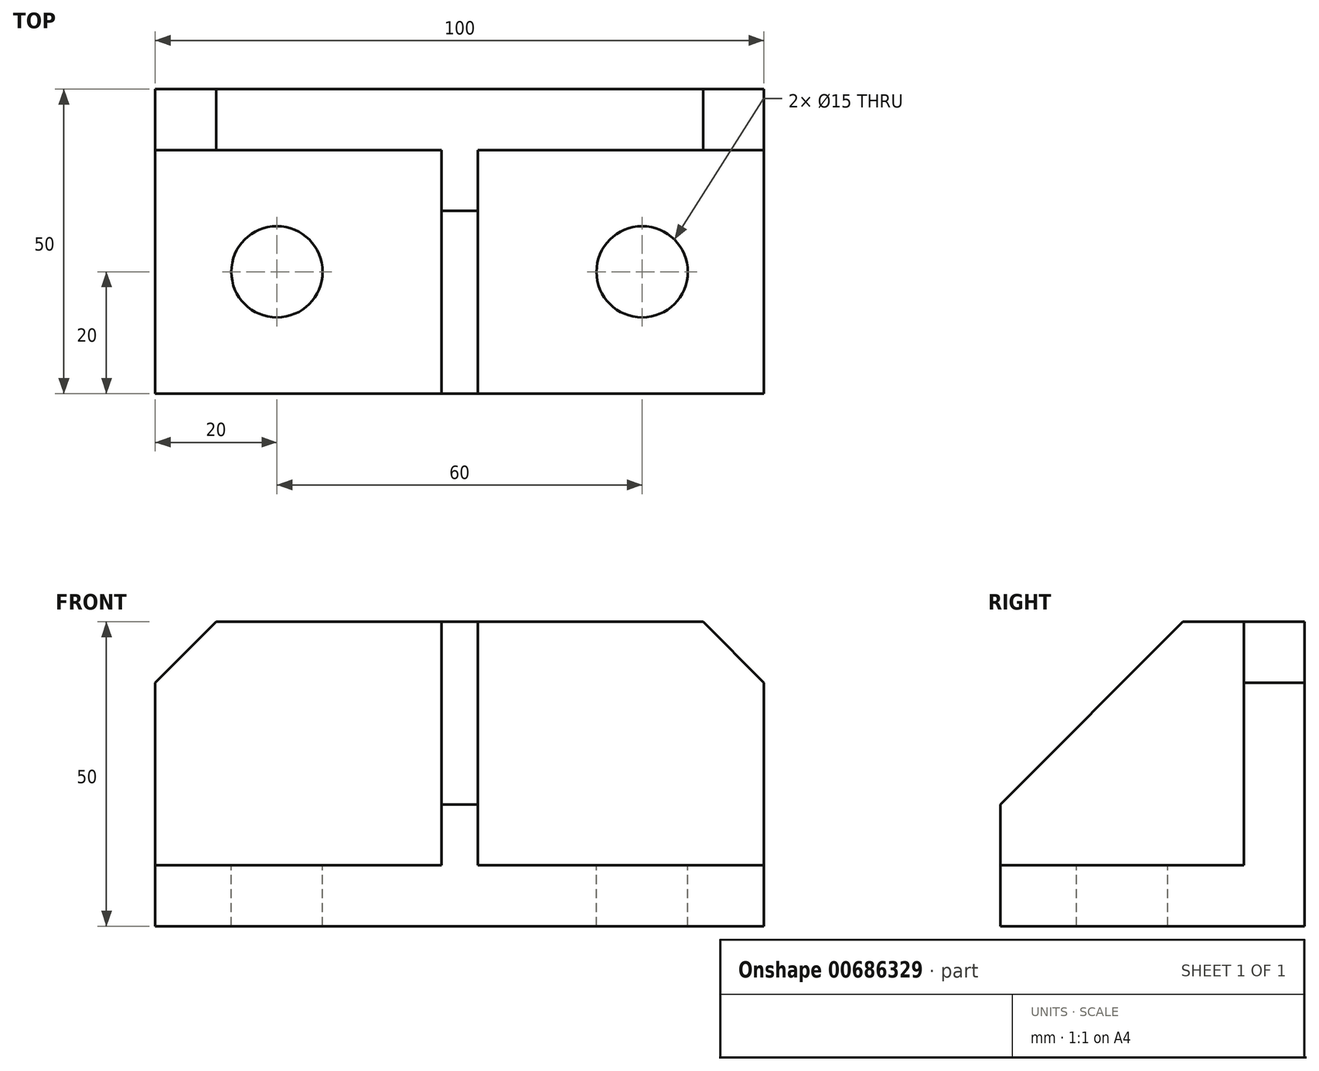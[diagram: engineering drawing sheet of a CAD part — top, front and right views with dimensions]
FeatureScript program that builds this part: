
annotation { "Feature Type Name" : "Feature", "Feature Type Description" : "" }
export const myFeature = defineFeature(function(context is Context, id is Id, definition is map)
    precondition{}
    {
        {
            var Q0;
            Q0=qCreatedBy(makeId("Front.planeOp"),FACE);
            var sketch = newSketch(context, id + "F0", { "sketchPlane" : qUnion([Q0])});
            skLineSegment(sketch, "E0.bottom", {"start": v(0, 0) * mm, "end": v(100, 0) * mm});
            skLineSegment(sketch, "E0.top", {"start": v(0, 50) * mm, "end": v(100, 50) * mm});
            skLineSegment(sketch, "E0.left", {"start": v(0, 0) * mm, "end": v(0, 50) * mm});
            skLineSegment(sketch, "E0.right", {"start": v(100, 0) * mm, "end": v(100, 50) * mm});
            skSolve(sketch);
        }
        {
            var Q0;
            Q0 = qSketchRegion(id + "F0", true);
            extrude(context, id + "F1", {"entities" : qUnion([Q0]), "depth" : 50 * mm, "offsetDistance" : 25 * mm});
        }
        {
            var Q0;
            Q0=makeQuery(id+"F1.opExtrude","CAP_FACE",FACE,{"disambiguationData":[OSD([sQuery(id+"F0.wireOp",EDGE,"E0.bottom"),sQuery(id+"F0.wireOp",EDGE,"E0.top"),sQuery(id+"F0.wireOp",EDGE,"E0.left"),sQuery(id+"F0.wireOp",EDGE,"E0.right")])],"isStart":false});
            var sketch = newSketch(context, id + "F2", { "sketchPlane" : qUnion([Q0])});
            skLineSegment(sketch, "E1.bottom", {"start": v(0, 50) * mm, "end": v(47, 50) * mm});
            skLineSegment(sketch, "E1.top", {"start": v(0, 10) * mm, "end": v(47, 10) * mm});
            skLineSegment(sketch, "E1.left", {"start": v(0, 50) * mm, "end": v(0, 10) * mm});
            skLineSegment(sketch, "E1.right", {"start": v(47, 50) * mm, "end": v(47, 10) * mm});
            skLineSegment(sketch, "E2.bottom", {"start": v(100, 50) * mm, "end": v(53, 50) * mm});
            skLineSegment(sketch, "E2.top", {"start": v(100, 10) * mm, "end": v(53, 10) * mm});
            skLineSegment(sketch, "E2.left", {"start": v(100, 50) * mm, "end": v(100, 10) * mm});
            skLineSegment(sketch, "E2.right", {"start": v(53, 50) * mm, "end": v(53, 10) * mm});
            skSolve(sketch);
        }
        {
            var Q0;
            Q0 = qSketchRegion(id + "F2", true);
            extrude(context, id + "F3", {"entities" : qUnion([Q0]), "operationType" : NewBodyOperationType.REMOVE, "oppositeDirection" : true, "depth" : 40 * mm, "offsetDistance" : 25 * mm});
        }
        {
            var Q0;
            Q0=makeQuery(id+"F1.opExtrude","CAP_EDGE",EDGE,{"disambiguationData":[OSD([sQuery(id+"F0.wireOp",EDGE,"E0.top")])],"isStart":false});
            chamfer(context, id + "F4", {"entities" : qUnion([Q0]), "width" : 30 * mm, "tangentPropagation" : true});
        }
        {
            var Q0;
            Q0=makeQuery(id+"F3.boolean.opBoolean","COPY",FACE,{"derivedFrom":makeQuery(id+"F3.opExtrude","SWEPT_FACE",FACE,{"disambiguationData":[OSD([sQuery(id+"F2.wireOp",EDGE,"E2.top")])]})});
            var sketch = newSketch(context, id + "F5", { "sketchPlane" : qUnion([Q0])});
            skCircle(sketch, "E3", {"center": v(20, -30) * mm, "radius": 7.5 * mm});
            skCircle(sketch, "E4", {"center": v(80, -30) * mm, "radius": 7.5 * mm});
            skSolve(sketch);
        }
        {
            var Q0;
            Q0 = qSketchRegion(id + "F5", true);
            extrude(context, id + "F6", {"entities" : qUnion([Q0]), "operationType" : NewBodyOperationType.REMOVE, "endBound" : BoundingType.THROUGH_ALL, "oppositeDirection" : true, "depth" : 30.3 * mm, "offsetDistance" : 25 * mm});
        }
        {
            var Q0;
            Q0=makeQuery(id+"F1.opExtrude","SWEPT_EDGE",EDGE,{"disambiguationData":[OSD([sQuery(id+"F0.wireOp",EDGE,"E0.top"),sQuery(id+"F0.wireOp",EDGE,"E0.right")])]});
            var Q1;
            Q1=makeQuery(id+"F1.opExtrude","SWEPT_EDGE",EDGE,{"disambiguationData":[OSD([sQuery(id+"F0.wireOp",EDGE,"E0.top"),sQuery(id+"F0.wireOp",EDGE,"E0.left")])]});
            chamfer(context, id + "F7", {"entities" : qUnion([Q0, Q1]), "width" : 10 * mm, "tangentPropagation" : true});
        }
    });
